# Revit family: VT.214
name_source: partatom
category: Арматура трубопроводов
revit_build: Autodesk Revit 2015 (Build: 20140606_1530(x64)
units: mm (PartAtom-declared; Revit-internal decimal feet)

## types (9) — shared parameters
Группа модели = VT.214
Изготовитель = VALTEC S.R.L.
Описание = Клапан шаровый полнопроходной

## per-type parameters (varying)
| type | 1 1/2" | 1 1/4" | 1" | 1/2" | 2 1/2" | 2" | 3" | 3/4" | 4" | A | G | Lрез | Lручки | Глубина вхождения | Код по классификатору | Сц |
| 3/4" | Нет | Нет | Нет | Нет | Нет | Нет | Нет | Да | Нет | 55 мм | 20 мм | 12 мм | 90 мм | 9 мм | VT.214.N.05 | 28 мм |
| 1/2" | Нет | Нет | Нет | Да | Нет | Нет | Нет | Нет | Нет | 48 мм | 15 мм | 10 мм | 90 мм | 8 мм | VT.214.N.04 | 23 мм |
| 1" | Нет | Нет | Да | Нет | Нет | Нет | Нет | Нет | Нет | 63 мм | 25 мм | 12 мм | 106 мм | 9 мм | VT.214.N.06 | 32 мм |
| 1 1/4" | Нет | Да | Нет | Нет | Нет | Нет | Нет | Нет | Нет | 77 мм | 32 мм | 15 мм | 122 мм | 12 мм | VT.214.N.07 | 40 мм |
| 1 1/2" | Да | Нет | Нет | Нет | Нет | Нет | Нет | Нет | Нет | 87 мм | 40 мм | 15 мм | 154 мм | 12 мм | VT.214.N.08 | 43 мм |
| 2" | Нет | Нет | Нет | Нет | Нет | Да | Нет | Нет | Нет | 101 мм | 50 мм | 15 мм | 153 мм | 12 мм | VT.214.N.09 | 50 мм |
| 2 1/2" | Нет | Нет | Нет | Нет | Да | Нет | Нет | Нет | Нет | 140 мм | 65 мм | 27 мм | 198 мм | 21 мм | VT.214.N.10 | 70 мм |
| 3" | Нет | Нет | Нет | Нет | Нет | Нет | Да | Нет | Нет | 153 мм | 80 мм | 27 мм | 235 мм | 21 мм | VT.214.N.11 | 77 мм |
| 4" | Нет | Нет | Нет | Нет | Нет | Нет | Нет | Нет | Да | 170 мм | 100 мм | 27 мм | 235 мм | 21 мм | VT.214.N.12 | 84 мм |
